# Revit family: Vent-Tee-PVC
name_source: partatom
category: Plumbing Fixtures
units: mm (PartAtom-declared; Revit-internal decimal feet)

## family parameters
Always vertical = Yes
Classification Number = 23.60.30.11.14
Cut with Voids When Loaded = No
Enable Cutting in Views = No
Maintain Annotation Orientation = No
Part Type = Normal
Room Calculation Point = No
Round Connector Dimension = Use Diameter
Shared = No
Work Plane-Based = Yes

## types (6) — shared parameters
Assembly Code = D2090900
CW Connection = No
Collar Thickness = 0' - 0 3/16"
Construction Details = http://www.arcat.com
Default Elevation = 4' - 0"
Description = PVC Vent Tee
Expected Lifespan (Years) = 40
Green Building-LEED = http://www.arcat.com
HW Connection = No
Keynote = 15000
Manufacturer = Generic
Manufacturer Fax = (203) 939-2444
Manufacturer Website = http://www.arcat.com
Model = Generic
Pipe Material = ARCAT - PVC - Schedule 80
Product Data = http://www.arcat.com
Product Properties = http://www.arcat.com
Specification = http://www.arcat.com
Vent Connection = Yes
Wall Thickness = 0' - 0 3/16"
Waste Connection = Yes
zero-valued in all types: Maintenance Schedule (Months), Warranty Duration (Years)

## per-type parameters (varying)
| type | Supply Connection Type |
| 1" | Plumbing-Connector : Weld-Weld - PVC-PVC 1 |
| 1-1/4" | Plumbing-Connector : Weld-Weld -PVC-PVC 125 |
| 1-1/2" | Plumbing-Connector : Weld-Weld -PVC-PVC 150 |
| 2" | Plumbing-Connector : Weld-Weld -PVC-PVC 2 |
| 3" | Plumbing-Connector : Weld-Weld -PVC-PVC 3 |
| 4" | Plumbing-Connector : Weld-Weld -PVC-PVC 3 |

## geometry (parser evidence)
native form markers: Sweep x6
no freeform markers — native parametric forms only
